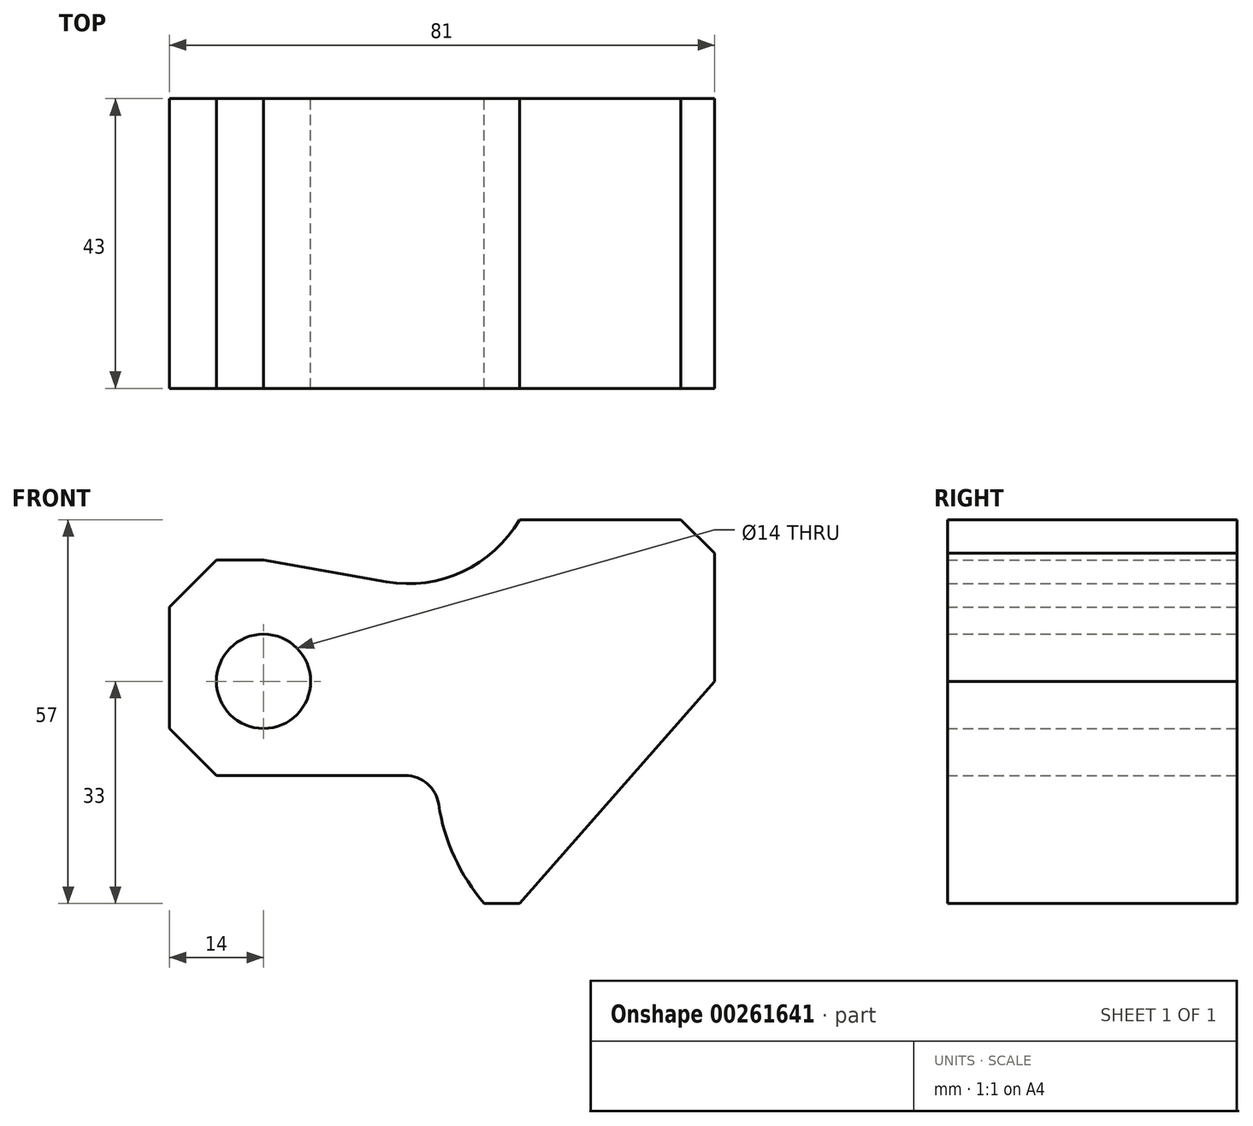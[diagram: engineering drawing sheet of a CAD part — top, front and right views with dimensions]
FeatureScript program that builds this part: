
annotation { "Feature Type Name" : "Feature", "Feature Type Description" : "" }
export const myFeature = defineFeature(function(context is Context, id is Id, definition is map)
    precondition{}
    {
        {
            var Q0;
            Q0=qCreatedBy(makeId("Front.planeOp"),FACE);
            var sketch = newSketch(context, id + "F0", { "sketchPlane" : qUnion([Q0])});
            skCircle(sketch, "E0", {"center": v(0, 0) * mm, "radius": 7 * mm});
            skLineSegment(sketch, "E1", {"start": v(0, 0) * mm, "end": v(0, -14) * mm});
            skLineSegment(sketch, "E2", {"start": v(0, -14) * mm, "end": v(-7, -14) * mm});
            skLineSegment(sketch, "E3", {"start": v(-7, -14) * mm, "end": v(-14, -7) * mm});
            skLineSegment(sketch, "E4", {"start": v(-14, -7) * mm, "end": v(-14, 11) * mm});
            skLineSegment(sketch, "E5", {"start": v(-14, 11) * mm, "end": v(-7, 18) * mm});
            skLineSegment(sketch, "E6", {"start": v(-7, 18) * mm, "end": v(0, 18) * mm});
            skLineSegment(sketch, "E7", {"start": v(0, 0) * mm, "end": v(0, 18) * mm});
            skLineSegment(sketch, "E8", {"start": v(0, 18) * mm, "end": v(18.24, 14.78) * mm});
            skLineSegment(sketch, "E9", {"start": v(0, 0) * mm, "end": v(7, 0) * mm});
            skArc(sketch, "E10", {"start": v(18.24, 14.78) * mm, "mid": v(29.57, 16.28) * mm, "end": v(38, 24) * mm});
            skLineSegment(sketch, "E11", {"start": v(67, 0) * mm, "end": v(67, 19) * mm});
            skLineSegment(sketch, "E12", {"start": v(62, 24) * mm, "end": v(38, 24) * mm});
            skLineSegment(sketch, "E13", {"start": v(67, 0) * mm, "end": v(38, -33) * mm});
            skLineSegment(sketch, "E14", {"start": v(0, -14) * mm, "end": v(21.07, -14) * mm});
            skArc(sketch, "E15", {"start": v(26.01, -18.26) * mm, "mid": v(28.35, -26.12) * mm, "end": v(32.79, -33) * mm});
            skLineSegment(sketch, "E16", {"start": v(38, -33) * mm, "end": v(32.79, -33) * mm});
            skPoint(sketch, "E17.visualSharp", {"position": v(25.7, -14) * mm});
            skArc(sketch, "E17.filletArc", {"start": v(26.01, -18.26) * mm, "mid": v(24.33, -15.21) * mm, "end": v(21.07, -14) * mm});
            skPoint(sketch, "E18.start.orphan", {"position": v(67, 24) * mm});
            skLineSegment(sketch, "E19", {"start": v(67, 19) * mm, "end": v(62, 24) * mm});
            skPoint(sketch, "E20.orphan", {"position": v(69.36, 24) * mm});
            skSolve(sketch);
        }
        {
            var Q0;
            Q0 = qSketchRegion(id + "F0", true);
            extrude(context, id + "F1", {"entities" : qUnion([Q0]), "depth" : 43 * mm});
        }
    });
